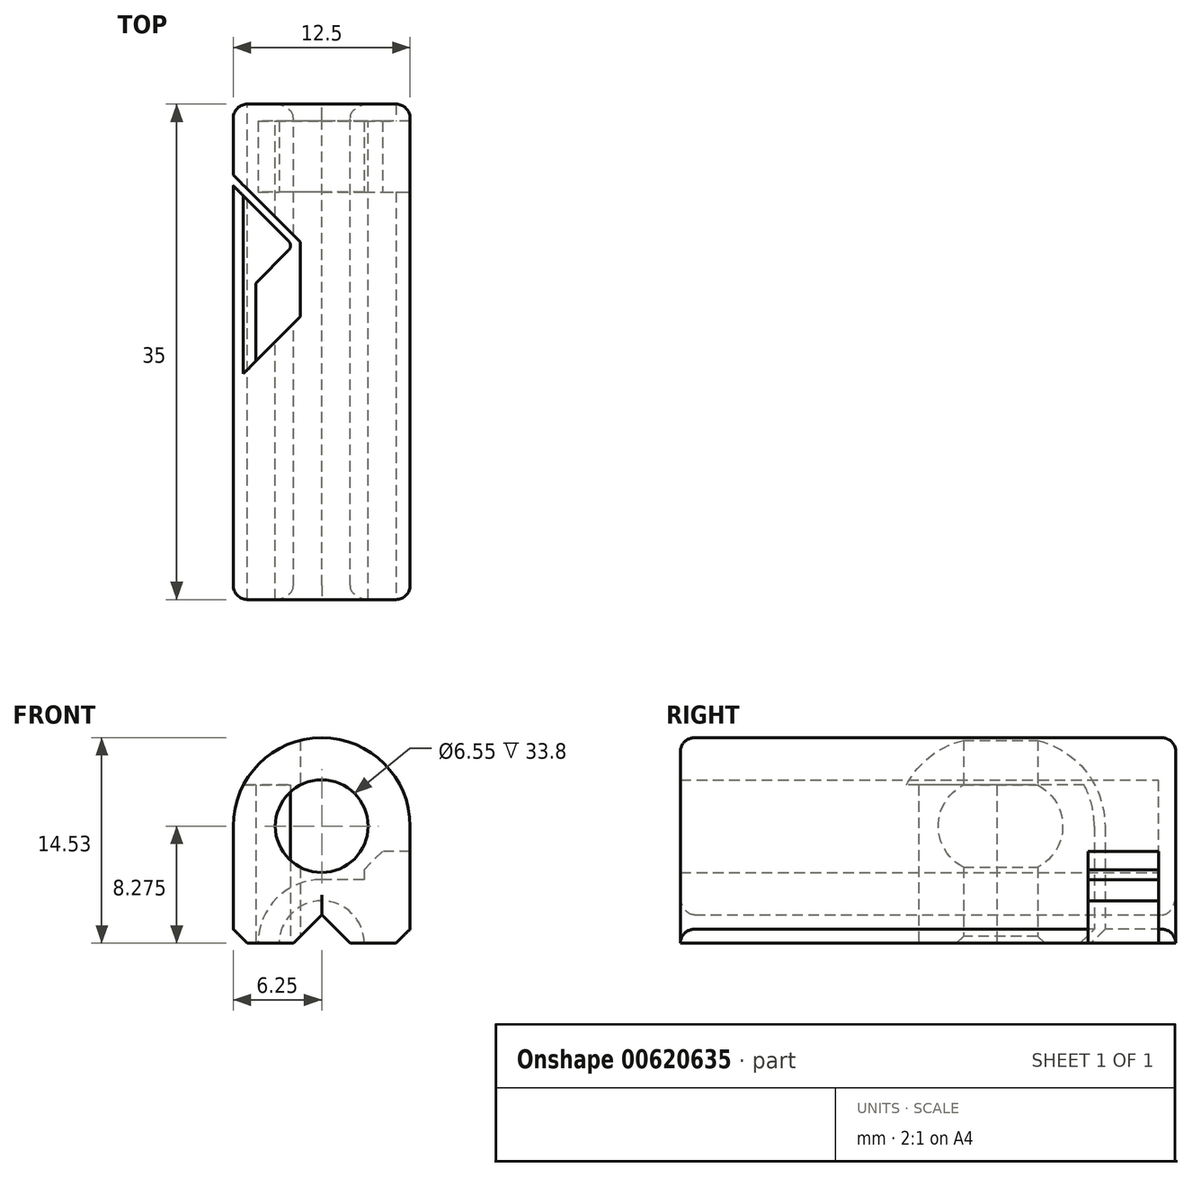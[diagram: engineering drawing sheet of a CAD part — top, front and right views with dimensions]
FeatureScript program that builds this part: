
annotation { "Feature Type Name" : "Feature", "Feature Type Description" : "" }
export const myFeature = defineFeature(function(context is Context, id is Id, definition is map)
    precondition{}
    {
        {
            var Q0;
            Q0=qCreatedBy(makeId("Front.planeOp"),FACE);
            var sketch = newSketch(context, id + "F0", { "sketchPlane" : qUnion([Q0])});
            skLineSegment(sketch, "E0.bottom", {"start": v(-6.25, 0) * mm, "end": v(-2, 0) * mm});
            skLineSegment(sketch, "E0.top", {"start": v(-6.25, 8.28) * mm, "end": v(6.25, 8.28) * mm, "construction": true});
            skLineSegment(sketch, "E0.left", {"start": v(-6.25, 0) * mm, "end": v(-6.25, 8.28) * mm});
            skLineSegment(sketch, "E0.right", {"start": v(6.25, 0) * mm, "end": v(6.25, 8.28) * mm});
            skPoint(sketch, "E0.middle", {"position": v(0, 4.14) * mm});
            skLineSegment(sketch, "E1", {"start": v(-2, 0) * mm, "end": v(0, 2) * mm});
            skLineSegment(sketch, "E2", {"start": v(0, 2) * mm, "end": v(2, 0) * mm});
            skArc(sketch, "E3", {"start": v(6.25, 8.28) * mm, "mid": v(0, 14.53) * mm, "end": v(-6.25, 8.28) * mm});
            skCircle(sketch, "E4", {"center": v(0, 8.28) * mm, "radius": 3.28 * mm});
            skLineSegment(sketch, "E5.trimOffspring", {"start": v(2, 0) * mm, "end": v(6.25, 0) * mm});
            skSolve(sketch);
        }
        {
            var Q0;
            Q0=makeQuery(id+"F0.imprint","IMPRINT",FACE,{"disambiguationData":[TD([[makeQuery(id+"F0.imprint","IMPRINT",EDGE,{"derivedFrom":sQuery(id+"F0.wireOp",EDGE,"E0.bottom")}),1.0]])]});
            extrude(context, id + "F1", {"entities" : qUnion([Q0]), "endBound" : BoundingType.SYMMETRIC, "depth" : 35 * mm, "offsetDistance" : 25 * mm});
        }
        {
            var Q0;
            Q0=makeQuery(id+"F1.opExtrude","SWEPT_FACE",FACE,{"disambiguationData":[OSD([sQuery(id+"F0.wireOp",EDGE,"E0.bottom")])]});
            var sketch = newSketch(context, id + "F2", { "sketchPlane" : qUnion([Q0])});
            skLineSegment(sketch, "E6", {"start": v(-6.25, 2.25) * mm, "end": v(-1.5, -2.5) * mm});
            skLineSegment(sketch, "E7", {"start": v(-1.5, -2.5) * mm, "end": v(-1.5, -7.75) * mm});
            skLineSegment(sketch, "E8", {"start": v(-1.5, -7.75) * mm, "end": v(-6.25, -12.5) * mm});
            skLineSegment(sketch, "E9", {"start": v(-6.25, -12.5) * mm, "end": v(-6.25, 2.25) * mm});
            skSolve(sketch);
        }
        {
            var Q0;
            Q0 = qSketchRegion(id + "F2", true);
            extrude(context, id + "F3", {"entities" : qUnion([Q0]), "operationType" : NewBodyOperationType.REMOVE, "endBound" : BoundingType.THROUGH_ALL, "oppositeDirection" : true, "depth" : 25 * mm, "offsetDistance" : 25 * mm});
        }
        {
            var Q0;
            Q0=makeQuery(id+"F1.opExtrude","SWEPT_FACE",FACE,{"disambiguationData":[OSD([sQuery(id+"F0.wireOp",EDGE,"E0.bottom")])]});
            var sketch = newSketch(context, id + "F4", { "sketchPlane" : qUnion([Q0])});
            skLineSegment(sketch, "E10", {"start": v(-6.25, 2.25) * mm, "end": v(-6.25, -11.75) * mm});
            skLineSegment(sketch, "E11", {"start": v(-6.25, -11.75) * mm, "end": v(-2, -7.5) * mm});
            skLineSegment(sketch, "E12", {"start": v(-2, -7.5) * mm, "end": v(-4.65, -4.85) * mm});
            skLineSegment(sketch, "E13", {"start": v(-4.65, -4.85) * mm, "end": v(-4.65, 0.65) * mm});
            skLineSegment(sketch, "E14", {"start": v(-4.65, 0.65) * mm, "end": v(-6.25, 2.25) * mm});
            skSolve(sketch);
        }
        {
            var Q0;
            Q0 = qSketchRegion(id + "F4", true);
            var Q1;
            Q1=makeQuery(id+"F3.boolean.opBoolean","INTERSECT",VERTEX,{"disambiguationData":[OD(1.0)],"derivedFrom":[makeQuery(id+"F1.opExtrude","SWEPT_FACE",FACE,{"disambiguationData":[OSD([sQuery(id+"F0.wireOp",EDGE,"E4")])]}),makeQuery(id+"F3.opExtrude","SWEPT_FACE",FACE,{"disambiguationData":[OSD([sQuery(id+"F2.wireOp",EDGE,"E6")])]}),makeQuery(id+"F3.opExtrude","SWEPT_FACE",FACE,{"disambiguationData":[OSD([sQuery(id+"F2.wireOp",EDGE,"E7")])]})]});
            extrude(context, id + "F5", {"entities" : qUnion([Q0]), "operationType" : NewBodyOperationType.ADD, "endBound" : BoundingType.UP_TO_VERTEX, "oppositeDirection" : true, "depth" : 25 * mm, "endBoundEntityVertex" : qUnion([Q1]), "offsetDistance" : 25 * mm});
        }
        {
            var Q0;
            Q0=makeQuery(id+"F1.opExtrude","CAP_FACE",FACE,{"disambiguationData":[OSD([sQuery(id+"F0.wireOp",EDGE,"E0.bottom"),sQuery(id+"F0.wireOp",EDGE,"E0.left"),sQuery(id+"F0.wireOp",EDGE,"E0.right"),sQuery(id+"F0.wireOp",EDGE,"E1"),sQuery(id+"F0.wireOp",EDGE,"E2"),sQuery(id+"F0.wireOp",EDGE,"E3"),sQuery(id+"F0.wireOp",EDGE,"E4"),sQuery(id+"F0.wireOp",EDGE,"E5.trimOffspring")])],"isStart":false});
            var sketch = newSketch(context, id + "F6", { "sketchPlane" : qUnion([Q0])});
            skArc(sketch, "E15", {"start": v(-6.25, 8.28) * mm, "mid": v(-6.07, 9.77) * mm, "end": v(-5.53, 11.19) * mm});
            skLineSegment(sketch, "E16", {"start": v(-6.25, 8.28) * mm, "end": v(-6.25, 11.19) * mm});
            skLineSegment(sketch, "E17", {"start": v(-6.25, 11.19) * mm, "end": v(-5.53, 11.19) * mm});
            skSolve(sketch);
        }
        {
            var Q0;
            Q0 = qSketchRegion(id + "F6", true);
            extrude(context, id + "F7", {"entities" : qUnion([Q0]), "operationType" : NewBodyOperationType.REMOVE, "endBound" : BoundingType.THROUGH_ALL, "oppositeDirection" : true, "depth" : 25 * mm, "offsetDistance" : 25 * mm});
        }
        {
            var Q0;
            Q0=makeQuery(id+"F5.opExtrude","SWEPT_EDGE",EDGE,{"disambiguationData":[OSD([sQuery(id+"F4.wireOp",EDGE,"E11"),sQuery(id+"F4.wireOp",EDGE,"E12")])]});
            fillet(context, id + "F8", {"entities" : qUnion([Q0]), "radius" : 0.5 * mm, "tangentPropagation" : true, "allowEdgeOverflow" : false});
        }
        {
            var Q0;
            Q0=makeQuery(id+"F1.opExtrude","SWEPT_FACE",FACE,{"disambiguationData":[OSD([sQuery(id+"F0.wireOp",EDGE,"E5.trimOffspring")])]});
            var sketch = newSketch(context, id + "F9", { "sketchPlane" : qUnion([Q0])});
            skLineSegment(sketch, "E18", {"start": v(0, -25.95) * mm, "end": v(0, 25.43) * mm});
            skLineSegment(sketch, "E19.bottom", {"start": v(-3, -16.3) * mm, "end": v(-4.5, -16.3) * mm});
            skLineSegment(sketch, "E19.top", {"start": v(-3, -11.3) * mm, "end": v(-4.5, -11.3) * mm});
            skLineSegment(sketch, "E19.left", {"start": v(-3, -16.3) * mm, "end": v(-3, -11.3) * mm});
            skLineSegment(sketch, "E19.right", {"start": v(-4.5, -16.3) * mm, "end": v(-4.5, -11.3) * mm});
            skSolve(sketch);
        }
        {
            var Q0;
            Q0=makeQuery(id+"F9.imprint","IMPRINT",FACE,{"disambiguationData":[TD([[makeQuery(id+"F9.imprint","IMPRINT",EDGE,{"derivedFrom":sQuery(id+"F9.wireOp",EDGE,"E19.bottom")}),-1.0]])]});
            var Q1;
            Q1=makeQuery(id+"F9.imprint","IMPRINT",FACE,{"disambiguationData":[TD([[makeQuery(id+"F9.imprint","IMPRINT",EDGE,{"derivedFrom":sQuery(id+"F9.wireOp",EDGE,"nibdCGtx-oTkS-gW6R-p9rg-CtCcHbBoDCIT.bottom")}),-1.0]])]});
            var Q2;
            Q2=sQuery(id+"F9.wireOp",EDGE,"E18");
            revolve(context, id + "F10", {"operationType" : NewBodyOperationType.REMOVE, "entities" : qUnion([Q0, Q1]), "axis" : qUnion([Q2]), "revolveType" : RevolveType.FULL, "oppositeDirection" : true});
        }
        {
            var Q0;
            Q0=makeQuery(id+"F10.boolean.opBoolean","COPY",FACE,{"derivedFrom":makeQuery(id+"F10.opRevolve","SWEPT_FACE",FACE,{"disambiguationData":[OSD([sQuery(id+"F9.wireOp",EDGE,"E19.top")])]})});
            var sketch = newSketch(context, id + "F11", { "sketchPlane" : qUnion([Q0])});
            skLineSegment(sketch, "E20", {"start": v(0, 4.5) * mm, "end": v(-3, 4.5) * mm});
            skLineSegment(sketch, "E21", {"start": v(-6.25, 4.5) * mm, "end": v(-6.25, 0) * mm});
            skLineSegment(sketch, "E22", {"start": v(-6.25, 0) * mm, "end": v(-4.5, 0) * mm});
            skArc(sketch, "E23", {"start": v(0, 4.5) * mm, "mid": v(-3.18, 3.18) * mm, "end": v(-4.5, 0) * mm});
            skLineSegment(sketch, "E24", {"start": v(-3, 4.5) * mm, "end": v(-3, 5.2) * mm});
            skLineSegment(sketch, "E25", {"start": v(-4.3, 6.5) * mm, "end": v(-6.25, 6.5) * mm});
            skLineSegment(sketch, "E26", {"start": v(-6.25, 6.5) * mm, "end": v(-6.25, 4.5) * mm});
            skLineSegment(sketch, "E27", {"start": v(-3, 5.2) * mm, "end": v(-4.3, 6.5) * mm});
            skSolve(sketch);
        }
        {
            var Q0;
            Q0 = qSketchRegion(id + "F11", true);
            var Q1;
            Q1=makeQuery(id+"F10.boolean.opBoolean","COPY",FACE,{"derivedFrom":makeQuery(id+"F10.opRevolve","SWEPT_FACE",FACE,{"disambiguationData":[OSD([sQuery(id+"F9.wireOp",EDGE,"E19.bottom")])]})});
            extrude(context, id + "F12", {"entities" : qUnion([Q0]), "operationType" : NewBodyOperationType.REMOVE, "endBound" : BoundingType.UP_TO_SURFACE, "depth" : 25 * mm, "endBoundEntityFace" : qUnion([Q1]), "offsetDistance" : 25 * mm});
        }
        {
            var Q0;
            {var subQ0=sQuery(id+"F0.wireOp",EDGE,"E0.bottom");var subQ1=sQuery(id+"F0.wireOp",EDGE,"E0.left");Q0=makeQuery(id+"F3.boolean.opBoolean","SPLIT",EDGE,{"disambiguationData":[TD([makeQuery(id+"F3.opExtrude","SWEPT_FACE",FACE,{"disambiguationData":[OSD([sQuery(id+"F2.wireOp",EDGE,"E8")])]})])],"derivedFrom":makeQuery(id+"F1.opExtrude","SWEPT_EDGE",EDGE,{"disambiguationData":[OSD([subQ0,subQ1])]})});}
            var Q1;
            {var subQ0=sQuery(id+"F0.wireOp",EDGE,"E0.bottom");var subQ1=sQuery(id+"F0.wireOp",EDGE,"E0.left");Q1=makeQuery(id+"F5.boolean.opBoolean","MERGE",EDGE,{"derivedFrom":[makeQuery(id+"F3.boolean.opBoolean","SPLIT",EDGE,{"disambiguationData":[TD([makeQuery(id+"F3.opExtrude","SWEPT_FACE",FACE,{"disambiguationData":[OSD([sQuery(id+"F2.wireOp",EDGE,"E6")])]})])],"derivedFrom":makeQuery(id+"F1.opExtrude","SWEPT_EDGE",EDGE,{"disambiguationData":[OSD([subQ0,subQ1])]})}),makeQuery(id+"F5.opExtrude","CAP_EDGE",EDGE,{"disambiguationData":[OSD([sQuery(id+"F4.wireOp",EDGE,"E10")])],"isStart":true})]});}
            var Q2;
            {var subQ0=sQuery(id+"F9.wireOp",EDGE,"E19.bottom");var subQ1=sQuery(id+"F0.wireOp",EDGE,"E5.trimOffspring");var subQ3=sQuery(id+"F0.wireOp",EDGE,"E0.right");Q2=makeQuery(id+"FVVOsy0JL4eOBj7_1.1.F12.boolean.opBoolean","SPLIT",EDGE,{"disambiguationData":[TD([makeQuery(id+"FVVOsy0JL4eOBj7_1.1.F10.boolean.opBoolean","COPY",FACE,{"derivedFrom":makeQuery(id+"FVVOsy0JL4eOBj7_1.1.F10.opRevolve","SWEPT_FACE",FACE,{"disambiguationData":[OSD([subQ0])]})})])],"derivedFrom":makeQuery(id+"F12.boolean.opBoolean","SPLIT",EDGE,{"disambiguationData":[TD([makeQuery(id+"F10.boolean.opBoolean","COPY",FACE,{"derivedFrom":makeQuery(id+"F10.opRevolve","SWEPT_FACE",FACE,{"disambiguationData":[OSD([sQuery(id+"F9.wireOp",EDGE,"E19.top")])]})})])],"derivedFrom":makeQuery(id+"F1.opExtrude","SWEPT_EDGE",EDGE,{"disambiguationData":[OSD([subQ3,subQ1])]})})});}
            var Q3;
            {var subQ0=sQuery(id+"F9.wireOp",EDGE,"E19.top");var subQ1=makeQuery(id+"F10.boolean.opBoolean","COPY",FACE,{"derivedFrom":makeQuery(id+"F10.opRevolve","SWEPT_FACE",FACE,{"disambiguationData":[OSD([subQ0])]})});var subQ7=sQuery(id+"F0.wireOp",EDGE,"E5.trimOffspring");var subQ9=sQuery(id+"F0.wireOp",EDGE,"E0.right");Q3=makeQuery(id+"FVVOsy0JL4eOBj7_1.1.F12.boolean.opBoolean","SPLIT",EDGE,{"disambiguationData":[TD([subQ1])],"derivedFrom":makeQuery(id+"F12.boolean.opBoolean","SPLIT",EDGE,{"disambiguationData":[TD([subQ1])],"derivedFrom":makeQuery(id+"F1.opExtrude","SWEPT_EDGE",EDGE,{"disambiguationData":[OSD([subQ9,subQ7])]})})});}
            var Q4;
            {var subQ0=sQuery(id+"F9.wireOp",EDGE,"E19.bottom");var subQ1=sQuery(id+"F0.wireOp",EDGE,"E5.trimOffspring");var subQ2=sQuery(id+"F0.wireOp",EDGE,"E0.right");Q4=makeQuery(id+"F12.boolean.opBoolean","SPLIT",EDGE,{"disambiguationData":[TD([makeQuery(id+"F10.boolean.opBoolean","COPY",FACE,{"derivedFrom":makeQuery(id+"F10.opRevolve","SWEPT_FACE",FACE,{"disambiguationData":[OSD([subQ0])]})})])],"derivedFrom":makeQuery(id+"F1.opExtrude","SWEPT_EDGE",EDGE,{"disambiguationData":[OSD([subQ2,subQ1])]})});}
            chamfer(context, id + "F13", {"entities" : qUnion([Q0, Q1, Q2, Q3, Q4]), "width" : 1 * mm, "tangentPropagation" : true});
        }
        {
            var Q0;
            Q0=makeQuery(id+"F1.opExtrude","CAP_EDGE",EDGE,{"disambiguationData":[OSD([sQuery(id+"F0.wireOp",EDGE,"E1")])],"isStart":true});
            var Q1;
            Q1=makeQuery(id+"F1.opExtrude","CAP_EDGE",EDGE,{"disambiguationData":[OSD([sQuery(id+"F0.wireOp",EDGE,"E2")])],"isStart":true});
            var Q2;
            Q2=makeQuery(id+"F1.opExtrude","CAP_EDGE",EDGE,{"disambiguationData":[OSD([sQuery(id+"F0.wireOp",EDGE,"E1")])],"isStart":false});
            var Q3;
            Q3=makeQuery(id+"F1.opExtrude","CAP_EDGE",EDGE,{"disambiguationData":[OSD([sQuery(id+"F0.wireOp",EDGE,"E2")])],"isStart":false});
            var Q4;
            Q4=makeQuery(id+"F1.opExtrude","CAP_EDGE",EDGE,{"disambiguationData":[OSD([sQuery(id+"F0.wireOp",EDGE,"E0.left")])],"isStart":true});
            var Q5;
            Q5=makeQuery(id+"F1.opExtrude","CAP_EDGE",EDGE,{"disambiguationData":[OSD([sQuery(id+"F0.wireOp",EDGE,"E3")])],"isStart":false});
            fillet(context, id + "F14", {"entities" : qUnion([Q0, Q1, Q2, Q3, Q4, Q5]), "radius" : 1 * mm, "tangentPropagation" : true, "allowEdgeOverflow" : false});
        }
        {
            var Q0;
            Q0=makeQuery(id+"F1.opExtrude","CAP_FACE",FACE,{"disambiguationData":[OSD([sQuery(id+"F0.wireOp",EDGE,"E0.bottom"),sQuery(id+"F0.wireOp",EDGE,"E0.left"),sQuery(id+"F0.wireOp",EDGE,"E0.right"),sQuery(id+"F0.wireOp",EDGE,"E1"),sQuery(id+"F0.wireOp",EDGE,"E2"),sQuery(id+"F0.wireOp",EDGE,"E3"),sQuery(id+"F0.wireOp",EDGE,"E4"),sQuery(id+"F0.wireOp",EDGE,"E5.trimOffspring")])],"isStart":true});
            var sketch = newSketch(context, id + "F15", { "sketchPlane" : qUnion([Q0])});
            skCircle(sketch, "E28", {"center": v(0, 8.28) * mm, "radius": 3.28 * mm});
            skSolve(sketch);
        }
        {
            var Q0;
            Q0 = qSketchRegion(id + "F15", true);
            extrude(context, id + "F16", {"entities" : qUnion([Q0]), "operationType" : NewBodyOperationType.ADD, "oppositeDirection" : true, "depth" : 1.2 * mm, "offsetDistance" : 25 * mm});
        }
    });
